# Revit family: Sanitary_Toilet-Cisterns_hansgrohe_60110XXX-hansgrohe-Tank-with-bottom-wate__
name_source: partatom
category: Plumbing Fixtures
revit_build: Autodesk Revit 2018 (Build: 20170223_1515(x64)
units: mm (PartAtom-declared; Revit-internal decimal feet)

## family parameters
Always vertical = No
Cut with Voids When Loaded = No
OmniClass Number = 23.31.19.19.19
OmniClass Title = Water Closet Tanks
Part Type = Normal
Room Calculation Point = No
Round Connector Dimension = Use Diameter
Shared = No
Work Plane-Based = Yes

## types (1)
- 450 White
    Always visible = Yes
    BIMobject category = Toilet Cisterns
    Connector Description = Cold Water Inlet 12.7 mm
    Default Elevation = 1219.2 mm  [stored 4 ft]
    Description = hansgrohe Tank with bottom water supply
    Design country = Germany
    Diameter = 13 mm
    EAN code = 4059625478929
    Edition number = 1
    IFC Classification = Sanitary Terminal
    Manufacturer = Hansgrohe
    Manufacturer country = Germany
    Manufacturer name = hansgrohe
    Masterformat 2014 Code = 22 41 13
    Masterformat 2014 Description = Residential Water Closets, Urinals, and Bidets
    Material 1 = Hansgrohe - Ceramic - 450 White
    Material 2 = Hansgrohe - Metal - Chrome
    Model = 60110XXX
    OmniClass Code = 23-31 19 19 19
    OmniClass Description = Water Closet Tanks
    Product Guid = f00f3851-42f9-4920-9567-de215d0945c6
    Product SKU = 60110XXX
    Product data url = https://bimobject.com
    Product family = hansgrohe
    Product group = top mounted cisterns
    Product name = 60110XXX hansgrohe Tank with bottom water supply
    Product url = https://pro.hansgrohe.com
    QR code = https://bimobject.com
    URL = https://www.hansgrohe.com
    Uniclass 2015 Code = Pr_40_20_93_89
    Uniclass 2015 Name = WC cisterns
    Uniformat II Code = D2010
    Uniformat II Description = Plumbing Fixtures
    Weight Net (Kg) = 12

note: [stored X ft] marks values corroborated as IEEE doubles in the binary element streams (Revit-internal decimal feet)

## geometry (parser evidence)
native form markers: Sweep x3
no freeform markers — native parametric forms only
